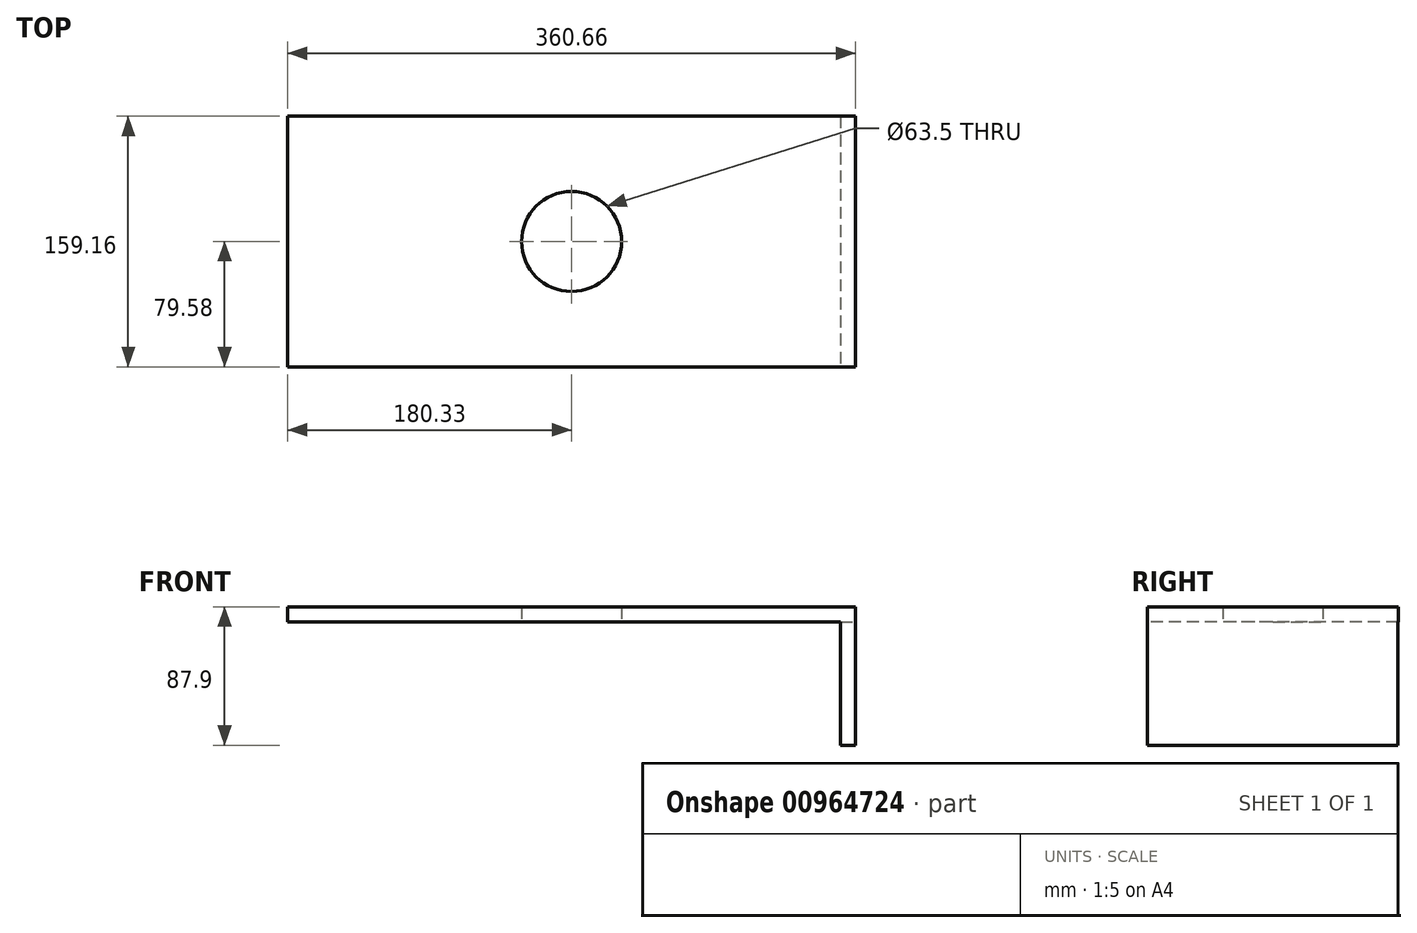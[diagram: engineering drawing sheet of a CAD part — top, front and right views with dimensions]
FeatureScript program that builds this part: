
annotation { "Feature Type Name" : "Feature", "Feature Type Description" : "" }
export const myFeature = defineFeature(function(context is Context, id is Id, definition is map)
    precondition{}
    {
        {
            var Q0;
            Q0=qCreatedBy(makeId("Top.planeOp"),FACE);
            var sketch = newSketch(context, id + "F0", { "sketchPlane" : qUnion([Q0])});
            skLineSegment(sketch, "E0.bottom", {"start": v(-180.33, 79.58) * mm, "end": v(180.33, 79.58) * mm});
            skLineSegment(sketch, "E0.top", {"start": v(-180.33, -79.58) * mm, "end": v(180.33, -79.58) * mm});
            skLineSegment(sketch, "E0.left", {"start": v(-180.33, 79.58) * mm, "end": v(-180.33, -79.58) * mm});
            skLineSegment(sketch, "E0.right", {"start": v(180.33, 79.58) * mm, "end": v(180.33, -79.58) * mm});
            skPoint(sketch, "E0.middle", {"position": v(0, 0) * mm});
            skSolve(sketch);
        }
        {
            var Q0;
            Q0=makeQuery(id+"F0.imprint","IMPRINT",FACE,{"disambiguationData":[TD([[makeQuery(id+"F0.imprint","IMPRINT",EDGE,{"derivedFrom":sQuery(id+"F0.wireOp",EDGE,"E0.bottom")}),-1.0]])]});
            extrude(context, id + "F1", {"entities" : qUnion([Q0]), "depth" : 9.52 * mm, "offsetDistance" : 25.4 * mm});
        }
        {
            var Q0;
            Q0=makeQuery(id+"F1.opExtrude","CAP_FACE",FACE,{"disambiguationData":[OSD([sQuery(id+"F0.wireOp",EDGE,"E0.bottom"),sQuery(id+"F0.wireOp",EDGE,"E0.top"),sQuery(id+"F0.wireOp",EDGE,"E0.left"),sQuery(id+"F0.wireOp",EDGE,"E0.right")])],"isStart":false});
            var sketch = newSketch(context, id + "F2", { "sketchPlane" : qUnion([Q0])});
            skCircle(sketch, "E1", {"center": v(0, 0) * mm, "radius": 39.77 * mm});
            skSolve(sketch);
        }
        {
            var Q0;
            Q0=sQuery(id+"F2.wireOp",VERTEX,"E1.center");
            var Q1;
            Q1=makeQuery(id+"F1.opExtrude","SWEPT_BODY",BODY,{"disambiguationData":[OSD([sQuery(id+"F0.wireOp",EDGE,"E0.bottom"),sQuery(id+"F0.wireOp",EDGE,"E0.top"),sQuery(id+"F0.wireOp",EDGE,"E0.left"),sQuery(id+"F0.wireOp",EDGE,"E0.right")])]});
            hole(context, id + "F3", {"style" : HoleStyle.SIMPLE, "endStyle" : HoleEndStyle.THROUGH, "holeDiameter" : 63.5 * mm, "majorDiameter" : 6.35 * mm, "isTappedThrough" : true, "tappedDepth" : 12.7 * mm, "tapClearance" : 3, "locations" : qUnion([Q0]), "scope" : qUnion([Q1]), "startStyle" : HoleStartStyle.SKETCH});
        }
        {
            var Q0;
            Q0=makeQuery(id+"F1.opExtrude","SWEPT_FACE",FACE,{"disambiguationData":[OSD([sQuery(id+"F0.wireOp",EDGE,"E0.right")])]});
            var sketch = newSketch(context, id + "F4", { "sketchPlane" : qUnion([Q0])});
            skLineSegment(sketch, "E2.bottom", {"start": v(-79.58, 0) * mm, "end": v(79.43, 0) * mm});
            skLineSegment(sketch, "E2.top", {"start": v(-79.58, -78.37) * mm, "end": v(79.43, -78.37) * mm});
            skLineSegment(sketch, "E2.left", {"start": v(-79.58, 0) * mm, "end": v(-79.58, -78.37) * mm});
            skLineSegment(sketch, "E2.right", {"start": v(79.43, 0) * mm, "end": v(79.43, -78.37) * mm});
            skLineSegment(sketch, "E3.bottom", {"start": v(-86.38, -38.6) * mm, "end": v(-103.95, -38.6) * mm});
            skLineSegment(sketch, "E3.top", {"start": v(-86.38, -50) * mm, "end": v(-103.95, -50) * mm});
            skLineSegment(sketch, "E3.left", {"start": v(-86.38, -38.6) * mm, "end": v(-86.38, -50) * mm});
            skLineSegment(sketch, "E3.right", {"start": v(-103.95, -38.6) * mm, "end": v(-103.95, -50) * mm});
            skSolve(sketch);
        }
        {
            var Q0;
            Q0=makeQuery(id+"F4.imprint","IMPRINT",FACE,{"disambiguationData":[TD([[makeQuery(id+"F4.imprint","IMPRINT",EDGE,{"derivedFrom":sQuery(id+"F4.wireOp",EDGE,"E2.bottom")}),1.0]])]});
            extrude(context, id + "F5", {"entities" : qUnion([Q0]), "operationType" : NewBodyOperationType.ADD, "oppositeDirection" : true, "depth" : 9.52 * mm, "offsetDistance" : 25.4 * mm});
        }
    });
